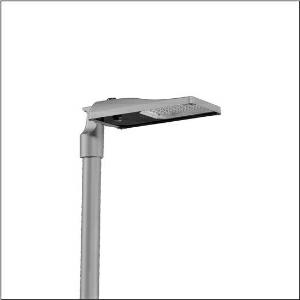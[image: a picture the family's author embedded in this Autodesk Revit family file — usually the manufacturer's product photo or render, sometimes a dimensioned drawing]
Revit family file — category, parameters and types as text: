
# Revit family: streetlight_sl_31_mini___pl52_5xh6h31t08ha_406f
name_source: partatom
category: Lighting Fixtures
units: mm (PartAtom-declared; Revit-internal decimal feet)

## family parameters
Cut with Voids When Loaded = No
Host = Face
Light Source = No
Part Type = Normal
Room Calculation Point = No
Round Connector Dimension = Use Diameter
Shared = No

## types (1)
- --- (1 x LED, 9070 lm, 68.3 W, 3000K)
    Apparent Load = 68 VA
    CIE Flux Codes = 27 59 98 100 100
    Color Rendering = 70
    Color Temperature = 3000K
    Default Elevation = 1800 mm
    Description = Streetlight SL 31 mini D4i, Desk-Remote mast luminaire for post-top, side-entry; light control with lens of PMMA; light distribution: PL52, direct asymmetric distribution, for standard-compliant lighting for roads and squares; LED: luminous flux: 9.070lm, light colour: 730, colour temperature: 3000K; luminous efficacy: 133lm/W; control: pre-setting: logarithmic dimming characteristic, flexible luminous flux parameterisation, time-dependent luminous flux control, constant luminous flux control, power reduction, intelligent temperature release in ECG and LED module, overheat protection; luminaire housing, of diecast aluminium, Siteco® metallic grey (DB 702S), corrosivity category C5 high according to DIN EN ISO 12944; cover of toughened safety glass, transparent, opened without tools; mast flange of diecast aluminium, Siteco® metallic grey (DB 702S), spigot size: 76/60mm, mast flange included unmounted; with cable H07RN-F 2x 1.5mm², cable length: 8,5m, connection cable pre-assembled; mains connection: 220..240V, AC, 50/60Hz; power consumption (at start of service life): 68,2W / (at end of service life): 74,4W / (with reduced operation 50%): 29,7W; protection rating (complete): IP66; insulation class (complete): insulation class II (safety insulation); impact resistance: IK09; certification: CE, ENEC, ENEC+, VDE, UKCA, ZD4i; permissible operating ambient temperature for outdoor applications: -40..+50°C; packaging unit: 1 piece

Light Distribution: PL52
    Height = 76 mm
    Lamp = 1 x LED
    Lamp Light Flux = 9070 lm
    Lamp Power = 68.3 W
    Lamp count = 1
    Length = 547 mm
    Luminous efficacy = 133 lm/W
    Manufacturer = Siteco
    ModVariant = No
    Model = 5XH6H31T08HA
    Number of Poles = 1
    OnlyDefault = Yes
    Power Factor = 1
    Product Name = Streetlight SL 31 mini | PL52
    Product group = mast luminaire | pylon top
    ProductGroupID = 6100
    Protection Class = Protection class II
    Protection Degree = IP 66
    RLX_Detail_Level = 1
    RLX_Emergency_Light_Flux = 0 lm
    RLX_Emergency_Type = 0
    RLX_Emergency_Type_DB = No
    RlxData = <blob elided: 33857 chars, md5=ae6f4d63>
    Socket = socket
    Standby Power = 0 W
    System Light Flux = 9070 lm
    System Power = 68 W
    Type Comments = factory setting: luminous flux: 100 % | dim-lin: 254 | 692 mA
    Type Image = l_1300332.jpg
    URL = http://relux.com
    VarID = @adj_002995
    Voltage = 0 V
    Weight = 0.00 kg
    Width = 265 mm

## geometry (parser evidence)
native form markers: Blend x4, Sweep x11
no freeform markers — native parametric forms only
